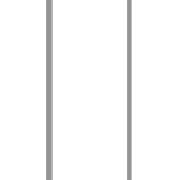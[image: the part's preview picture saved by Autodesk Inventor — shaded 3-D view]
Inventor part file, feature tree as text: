
AUTODESK INVENTOR PART (.ipt)
format: ipt  version: 2021 (Build 250183000, 183)  size: 151,040 bytes
history: native  units: in
note: dims shown in document units (in); Inventor stores cm internally (conversion verified against a paired STEP export)
features: plane x5, sketch x5, other x4, hole x1, extrude x1, boolean_combine x1
ambient origin geometry x8: Origin, YZ Plane, XZ Plane, XY Plane, X Axis, Y Axis, Z Axis, Center Point
bodies: Solid1 (feature_tree), Body (feature_tree), Solid2 (feature_tree)
feature tree (17):
  other  "Driven Length"
  other  "Frame Generator"
  plane  "Work Plane3"
  other  "Start Plane"
  other  "End Plane"
  hole  "Hole2"  [1 undecoded]
  plane  "Work Plane7"
  plane  "Work Plane8"
  plane  "Work Plane9"
  extrude  "Extrusion3"  Depth=0.0625in
  boolean_combine  "Combine1"
  sketch  "Sketch"  dims[d17=2.0in d18=0.12in d19=0.0in d22=1.5in d23=0.4375in d24=0.75in d25=0.635in d26=0.25in d27=0.5635in d28=1.0in d29=0.8108in d32=90.0deg d21=2.0in d34=0.12in d35=0.0in d8=0.5in d9=0.0344in d10=0.5in d11=0.0344in]
  sketch  "Sketch5"  dims[d0=1.5in d1=1.0in]
  sketch  "Sketch8"  dims[d2=0.0625in d3=0.0625in]
  plane  "Work Plane6"
  sketch  "Sketch9"  dims[d4=2.0in]
  sketch  "Sketch10"  dims[d16=-0.0in]
note: 1 required parameter value undecoded (feature->parameter linkage not recoverable at this tier; creation-order binding heuristic only, values carry confidence <= 0.55)
